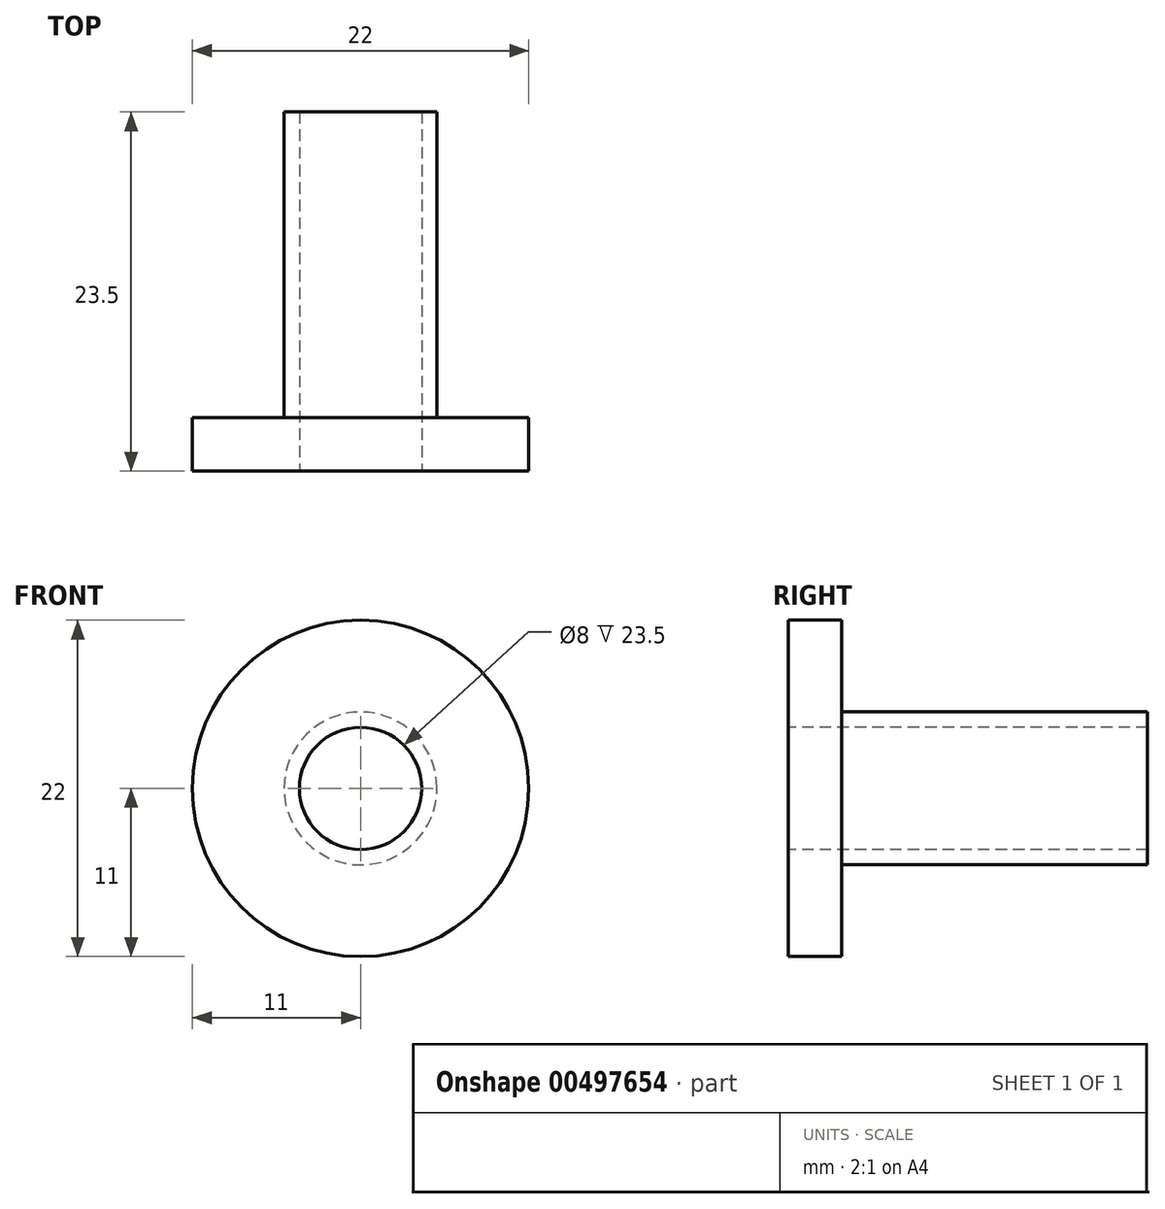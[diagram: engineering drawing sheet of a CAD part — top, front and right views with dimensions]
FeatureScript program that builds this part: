
annotation { "Feature Type Name" : "Feature", "Feature Type Description" : "" }
export const myFeature = defineFeature(function(context is Context, id is Id, definition is map)
    precondition{}
    {
        {
            var Q0;
            Q0=qCreatedBy(makeId("Front.planeOp"),FACE);
            var sketch = newSketch(context, id + "F0", { "sketchPlane" : qUnion([Q0])});
            skCircle(sketch, "E0", {"center": v(0, 0) * mm, "radius": 11 * mm});
            skSolve(sketch);
        }
        {
            var Q0;
            Q0=qSketchRegion(id+"F0",true);
            extrude(context, id + "F1", {"entities" : qUnion([Q0]), "depth" : 3.5 * mm});
        }
        {
            var Q0;
            Q0=makeQuery(id+"F1.opExtrude","CAP_FACE",FACE,{"disambiguationData":[OSD([sQuery(id+"F0.wireOp",EDGE,"E0")])],"isStart":true});
            var sketch = newSketch(context, id + "F2", { "sketchPlane" : qUnion([Q0])});
            skCircle(sketch, "E1", {"center": v(0, 0) * mm, "radius": 5 * mm});
            skSolve(sketch);
        }
        {
            var Q0;
            Q0=qSketchRegion(id+"F2",true);
            extrude(context, id + "F3", {"entities" : qUnion([Q0]), "operationType" : NewBodyOperationType.ADD, "depth" : 20 * mm});
        }
        {
            var Q0;
            Q0=makeQuery(id+"F1.opExtrude","CAP_FACE",FACE,{"disambiguationData":[OSD([sQuery(id+"F0.wireOp",EDGE,"E0")])],"isStart":false});
            var sketch = newSketch(context, id + "F4", { "sketchPlane" : qUnion([Q0])});
            skCircle(sketch, "E2", {"center": v(0, 0) * mm, "radius": 4 * mm});
            skSolve(sketch);
        }
        {
            var Q0;
            Q0=makeQuery(id+"F4.imprint","IMPRINT",FACE,{"disambiguationData":[TD([[makeQuery(id+"F4.imprint","IMPRINT",EDGE,{"derivedFrom":sQuery(id+"F4.wireOp",EDGE,"E2")}),1.0]])]});
            var Q1;
            Q1=sQuery(id+"F4.wireOp",EDGE,"E2");
            extrude(context, id + "F5", {"entities" : qUnion([Q0]), "operationType" : NewBodyOperationType.REMOVE, "surfaceEntities" : qUnion([Q1]), "oppositeDirection" : true, "depth" : 30 * mm});
        }
    });
